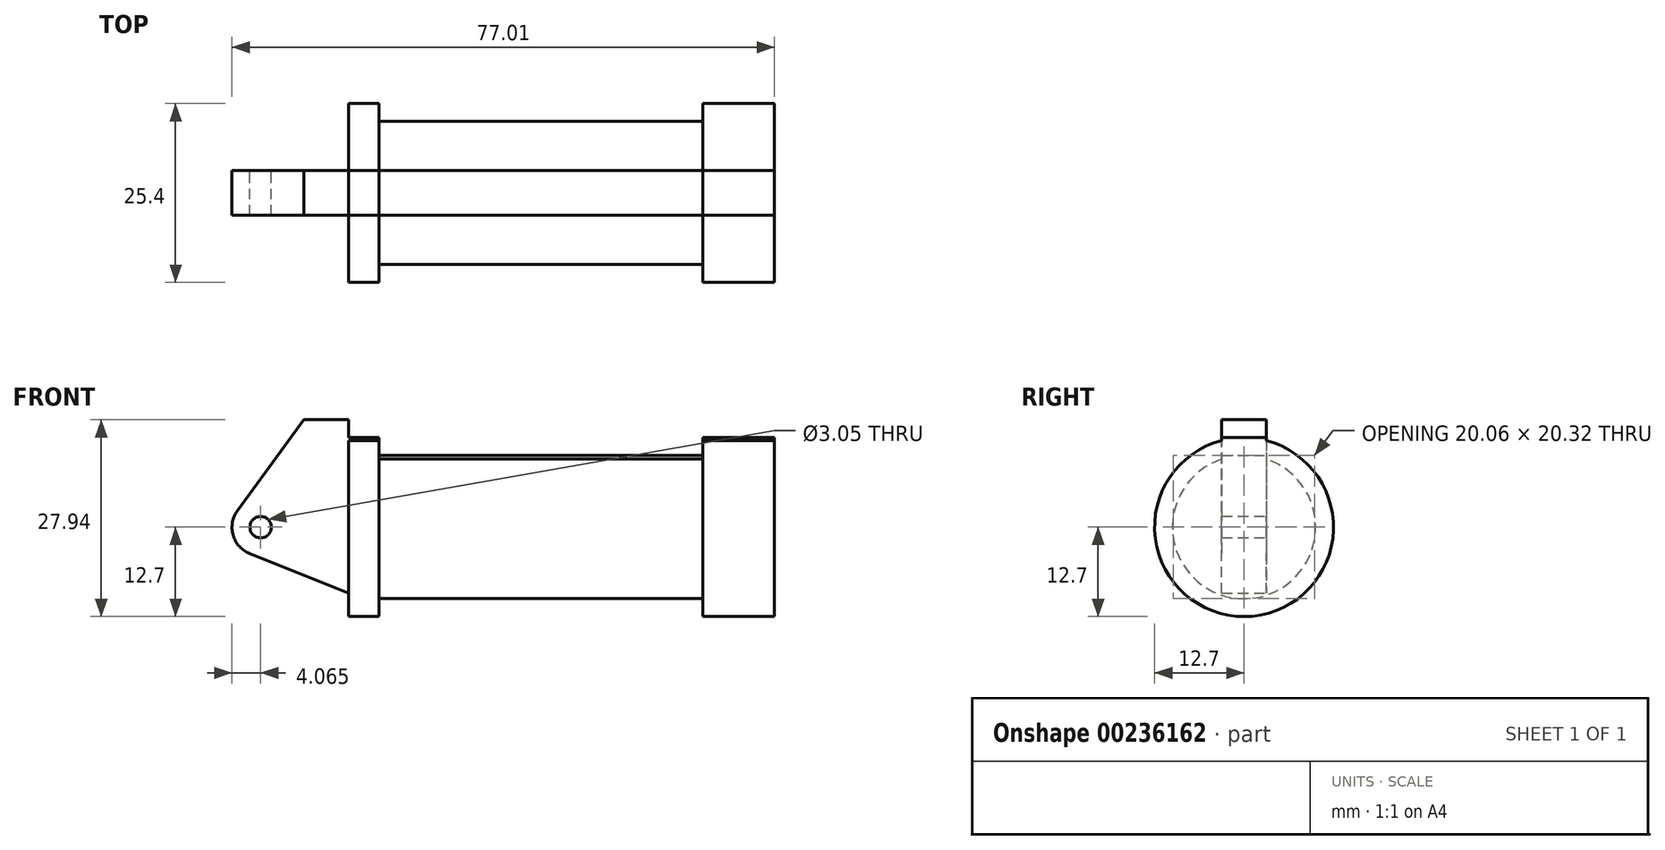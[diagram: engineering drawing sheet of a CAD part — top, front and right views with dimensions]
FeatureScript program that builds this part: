
annotation { "Feature Type Name" : "Feature", "Feature Type Description" : "" }
export const myFeature = defineFeature(function(context is Context, id is Id, definition is map)
    precondition{}
    {
        {
            var Q0;
            Q0=qCreatedBy(makeId("Front.planeOp"),FACE);
            var sketch = newSketch(context, id + "F0", { "sketchPlane" : qUnion([Q0])});
            skLineSegment(sketch, "E0", {"start": v(0, 0) * mm, "end": v(0, 12.7) * mm});
            skLineSegment(sketch, "E1", {"start": v(0, 12.7) * mm, "end": v(10.16, 12.7) * mm});
            skLineSegment(sketch, "E2", {"start": v(10.16, 12.7) * mm, "end": v(10.16, 10.16) * mm});
            skLineSegment(sketch, "E3", {"start": v(10.16, 10.16) * mm, "end": v(56.13, 10.16) * mm});
            skLineSegment(sketch, "E4", {"start": v(56.13, 10.16) * mm, "end": v(56.13, 12.7) * mm});
            skLineSegment(sketch, "E5", {"start": v(56.13, 12.7) * mm, "end": v(66.3, 12.7) * mm});
            skLineSegment(sketch, "E6", {"start": v(66.3, 12.7) * mm, "end": v(66.3, 0) * mm});
            skLineSegment(sketch, "E7", {"start": v(66.3, 0) * mm, "end": v(0, 0) * mm});
            skLineSegment(sketch, "E8", {"start": v(5.84, 15.24) * mm, "end": v(-0.5, 15.24) * mm});
            skLineSegment(sketch, "E9", {"start": v(-0.5, 15.24) * mm, "end": v(-9.93, 2.4) * mm});
            skLineSegment(sketch, "E10", {"start": v(0, 0) * mm, "end": v(-6.65, 0) * mm});
            skCircle(sketch, "E11", {"center": v(-6.65, 0) * mm, "radius": 4.06 * mm});
            skCircle(sketch, "E12", {"center": v(-6.65, 0) * mm, "radius": 1.52 * mm});
            skLineSegment(sketch, "E13", {"start": v(5.84, 15.24) * mm, "end": v(5.84, -9.4) * mm});
            skLineSegment(sketch, "E14", {"start": v(5.84, -9.4) * mm, "end": v(-8.17, -3.77) * mm});
            skSolve(sketch);
        }
        {
            var Q0;
            {var subQ0=sQuery(id+"F0.wireOp",EDGE,"E2");Q0=makeQuery(id+"F0.imprint","IMPRINT",FACE,{"disambiguationData":[TD([[makeQuery(id+"F0.imprint","IMPRINT",EDGE,{"derivedFrom":subQ0}),-1.0]])]});}
            var Q1;
            Q1=sQuery(id+"F0.wireOp",EDGE,"E7");
            revolve(context, id + "F1", {"entities" : qUnion([Q0]), "axis" : qUnion([Q1]), "revolveType" : RevolveType.FULL});
        }
        {
            var Q0;
            Q0 = qSketchRegion(id + "F0", true);
            extrude(context, id + "F2", {"entities" : qUnion([Q0]), "operationType" : NewBodyOperationType.ADD, "endBound" : BoundingType.SYMMETRIC, "depth" : 6.35 * mm});
        }
    });
